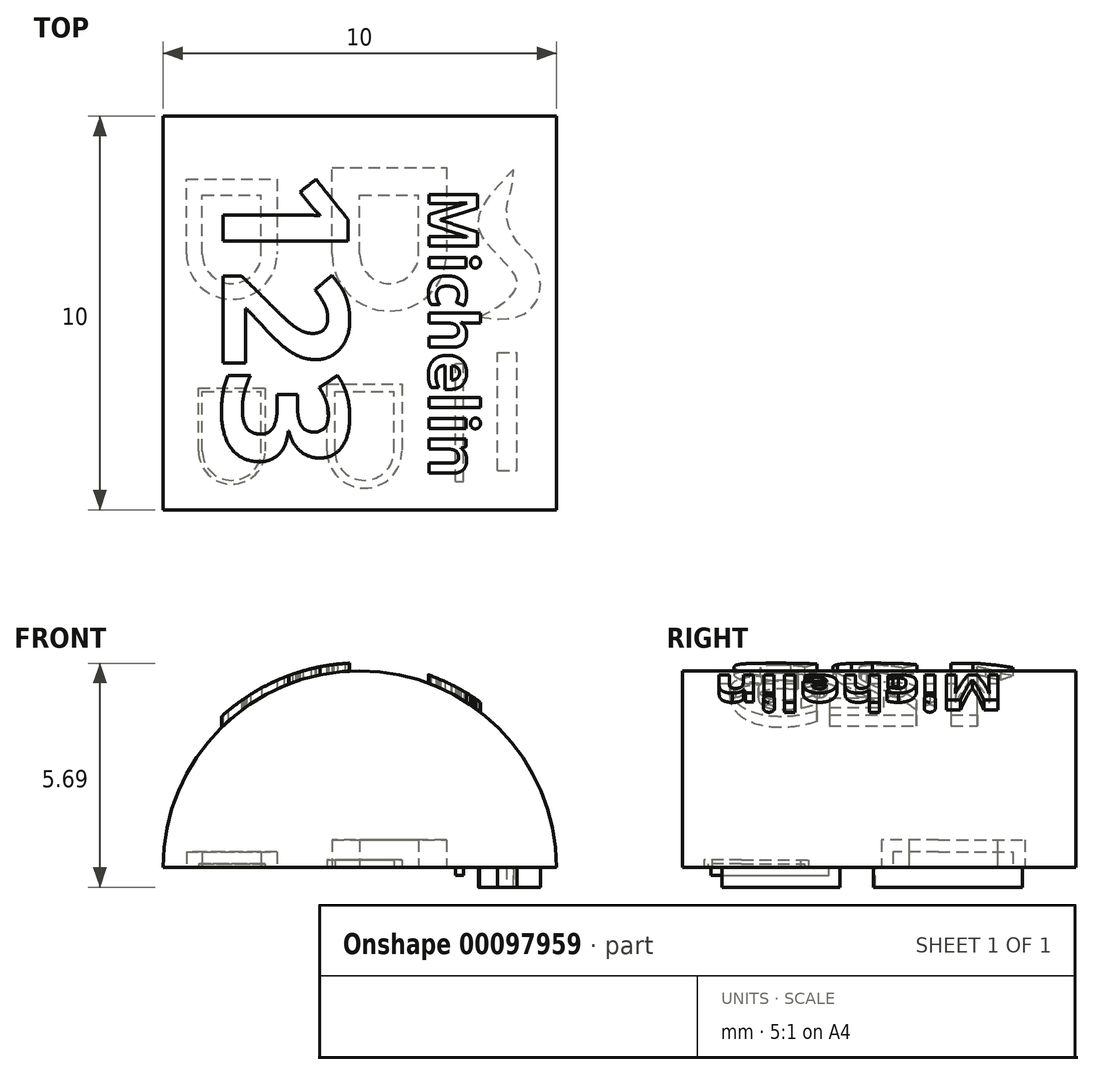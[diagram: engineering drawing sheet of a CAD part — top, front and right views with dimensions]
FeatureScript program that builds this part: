
annotation { "Feature Type Name" : "Feature", "Feature Type Description" : "" }
export const myFeature = defineFeature(function(context is Context, id is Id, definition is map)
    precondition{}
    {
        {
            var Q0;
            Q0=qCreatedBy(makeId("Front.planeOp"),FACE);
            var sketch = newSketch(context, id + "F0", { "sketchPlane" : qUnion([Q0])});
            skArc(sketch, "E0", {"start": v(-5, 0) * mm, "mid": v(0, 5) * mm, "end": v(5, 0) * mm});
            skLineSegment(sketch, "E1", {"start": v(-5, 0) * mm, "end": v(5, 0) * mm});
            skSolve(sketch);
        }
        {
            var Q0;
            Q0 = qSketchRegion(id + "F0", true);
            extrude(context, id + "F1", {"entities" : qUnion([Q0]), "depth" : 10 * mm});
        }
        {
            var Q0;
            Q0=makeQuery(id+"F1.opExtrude","CAP_FACE",FACE,{"disambiguationData":[OSD([sQuery(id+"F0.wireOp",EDGE,"E0"),sQuery(id+"F0.wireOp",EDGE,"E1")])],"isStart":false});
            var sketch = newSketch(context, id + "F2", { "sketchPlane" : qUnion([Q0])});
            skArc(sketch, "E2", {"start": v(-5.2, -0.07) * mm, "mid": v(-0.07, 5.2) * mm, "end": v(5.2, 0.07) * mm});
            skSolve(sketch);
        }
        {
            var Q0;
            Q0 = qSketchRegion(id + "F2", true);
            var Q1;
            Q1=sQuery(id+"F2.wireOp",EDGE,"E2");
            extrude(context, id + "F3", {"entities" : qUnion([Q0]), "bodyType" : ToolBodyType.SURFACE, "surfaceEntities" : qUnion([Q1]), "oppositeDirection" : true, "depth" : 10 * mm});
        }
        {
            var Q0;
            Q0=makeQuery(id+"F1.opExtrude","SWEPT_FACE",FACE,{"disambiguationData":[OSD([sQuery(id+"F0.wireOp",EDGE,"E1")])]});
            var sketch = newSketch(context, id + "F4", { "sketchPlane" : qUnion([Q0])});
            skLineSegment(sketch, "E3.top", {"start": v(-4, 7) * mm, "end": v(-2.5, 7) * mm});
            skLineSegment(sketch, "E3.left", {"start": v(-4, 8.5) * mm, "end": v(-4, 7) * mm});
            skLineSegment(sketch, "E4", {"start": v(-4.1, 8.5) * mm, "end": v(-4.1, 6.9) * mm});
            skLineSegment(sketch, "E5", {"start": v(-4.1, 6.9) * mm, "end": v(-2.4, 6.9) * mm});
            skLineSegment(sketch, "E6", {"start": v(-2.4, 6.9) * mm, "end": v(-2.4, 8.5) * mm});
            skLineSegment(sketch, "E7", {"start": v(-4.52, 8.5) * mm, "end": v(-2.4, 8.5) * mm, "construction": true});
            skLineSegment(sketch, "E8", {"start": v(-3.25, 8.9) * mm, "end": v(-3.25, 8.02) * mm, "construction": true});
            skArc(sketch, "E9", {"start": v(-4, 8.5) * mm, "mid": v(-3.25, 9.25) * mm, "end": v(-2.5, 8.5) * mm});
            skArc(sketch, "E10", {"start": v(-4.1, 8.5) * mm, "mid": v(-3.25, 9.35) * mm, "end": v(-2.4, 8.5) * mm});
            skLineSegment(sketch, "E11", {"start": v(-2.5, 8.5) * mm, "end": v(-2.5, 7) * mm});
            skSolve(sketch);
        }
        {
            var Q0;
            Q0=makeQuery(id+"F4.imprint","IMPRINT",FACE,{"disambiguationData":[TD([[makeQuery(id+"F4.imprint","IMPRINT",EDGE,{"derivedFrom":sQuery(id+"F4.wireOp",EDGE,"E3.top")}),-1.0]])]});
            extrude(context, id + "F5", {"entities" : qUnion([Q0]), "operationType" : NewBodyOperationType.REMOVE, "oppositeDirection" : true, "depth" : 0.1 * mm});
        }
        {
            var Q0;
            {var subQ0=sQuery(id+"F0.wireOp",EDGE,"E0");var subQ1=sQuery(id+"F0.wireOp",EDGE,"E1");Q0=makeQuery(id+"F5.boolean.opBoolean","SPLIT",FACE,{"disambiguationData":[TD([makeQuery(id+"F1.opExtrude","SWEPT_FACE",FACE,{"disambiguationData":[OSD([subQ0])]})])],"derivedFrom":makeQuery(id+"F1.opExtrude","SWEPT_FACE",FACE,{"disambiguationData":[OSD([subQ1])]})});}
            var sketch = newSketch(context, id + "F6", { "sketchPlane" : qUnion([Q0])});
            skLineSegment(sketch, "E12.top", {"start": v(-0.63, 7) * mm, "end": v(0.87, 7) * mm});
            skLineSegment(sketch, "E12.left", {"start": v(-0.63, 8.5) * mm, "end": v(-0.63, 7) * mm});
            skLineSegment(sketch, "E13", {"start": v(-0.83, 8.5) * mm, "end": v(-0.83, 6.8) * mm});
            skLineSegment(sketch, "E14", {"start": v(-0.83, 6.8) * mm, "end": v(1.07, 6.8) * mm});
            skLineSegment(sketch, "E15", {"start": v(1.07, 6.8) * mm, "end": v(1.07, 8.5) * mm});
            skLineSegment(sketch, "E16", {"start": v(-1.25, 8.5) * mm, "end": v(1.07, 8.5) * mm, "construction": true});
            skLineSegment(sketch, "E17", {"start": v(0.12, 8.8) * mm, "end": v(0.12, 7.92) * mm, "construction": true});
            skArc(sketch, "E18", {"start": v(-0.63, 8.5) * mm, "mid": v(0.12, 9.25) * mm, "end": v(0.87, 8.5) * mm});
            skArc(sketch, "E19", {"start": v(-0.83, 8.5) * mm, "mid": v(0.12, 9.45) * mm, "end": v(1.07, 8.5) * mm});
            skLineSegment(sketch, "E20", {"start": v(0.87, 8.5) * mm, "end": v(0.87, 7) * mm});
            skSolve(sketch);
        }
        {
            var Q0;
            Q0 = qSketchRegion(id + "F6", true);
            extrude(context, id + "F7", {"entities" : qUnion([Q0]), "operationType" : NewBodyOperationType.REMOVE, "oppositeDirection" : true, "depth" : 0.2 * mm});
        }
        {
            var Q0;
            {var subQ1=sQuery(id+"F0.wireOp",EDGE,"E0");var subQ2=makeQuery(id+"F1.opExtrude","SWEPT_FACE",FACE,{"disambiguationData":[OSD([subQ1])]});var subQ4=sQuery(id+"F0.wireOp",EDGE,"E1");Q0=makeQuery(id+"F7.boolean.opBoolean","SPLIT",FACE,{"disambiguationData":[TD([subQ2])],"derivedFrom":makeQuery(id+"F5.boolean.opBoolean","SPLIT",FACE,{"disambiguationData":[TD([subQ2])],"derivedFrom":makeQuery(id+"F1.opExtrude","SWEPT_FACE",FACE,{"disambiguationData":[OSD([subQ4])]})})});}
            var sketch = newSketch(context, id + "F8", { "sketchPlane" : qUnion([Q0])});
            skLineSegment(sketch, "E21.top", {"start": v(-4, 2) * mm, "end": v(-2.5, 2) * mm});
            skLineSegment(sketch, "E21.left", {"start": v(-4, 3.5) * mm, "end": v(-4, 2) * mm});
            skLineSegment(sketch, "E22", {"start": v(-4.4, 3.5) * mm, "end": v(-4.4, 1.6) * mm});
            skLineSegment(sketch, "E23", {"start": v(-4.4, 1.6) * mm, "end": v(-2.1, 1.6) * mm});
            skLineSegment(sketch, "E24", {"start": v(-2.1, 1.6) * mm, "end": v(-2.1, 3.5) * mm});
            skLineSegment(sketch, "E25", {"start": v(-3.84, 3.5) * mm, "end": v(-2.1, 3.5) * mm, "construction": true});
            skLineSegment(sketch, "E26", {"start": v(-3.25, 3.9) * mm, "end": v(-3.25, 3.02) * mm, "construction": true});
            skArc(sketch, "E27", {"start": v(-4, 3.5) * mm, "mid": v(-3.25, 4.25) * mm, "end": v(-2.5, 3.5) * mm});
            skArc(sketch, "E28", {"start": v(-4.4, 3.5) * mm, "mid": v(-3.25, 4.65) * mm, "end": v(-2.1, 3.5) * mm});
            skLineSegment(sketch, "E29", {"start": v(-2.5, 3.5) * mm, "end": v(-2.5, 2) * mm});
            skSolve(sketch);
        }
        {
            var Q0;
            Q0 = qSketchRegion(id + "F8", true);
            extrude(context, id + "F9", {"entities" : qUnion([Q0]), "operationType" : NewBodyOperationType.REMOVE, "oppositeDirection" : true, "depth" : 0.4 * mm});
        }
        {
            var Q0;
            {var subQ3=sQuery(id+"F0.wireOp",EDGE,"E0");var subQ4=makeQuery(id+"F1.opExtrude","SWEPT_FACE",FACE,{"disambiguationData":[OSD([subQ3])]});var subQ7=sQuery(id+"F0.wireOp",EDGE,"E1");Q0=makeQuery(id+"F9.boolean.opBoolean","SPLIT",FACE,{"disambiguationData":[TD([subQ4])],"derivedFrom":makeQuery(id+"F7.boolean.opBoolean","SPLIT",FACE,{"disambiguationData":[TD([subQ4])],"derivedFrom":makeQuery(id+"F5.boolean.opBoolean","SPLIT",FACE,{"disambiguationData":[TD([subQ4])],"derivedFrom":makeQuery(id+"F1.opExtrude","SWEPT_FACE",FACE,{"disambiguationData":[OSD([subQ7])]})})})});}
            var sketch = newSketch(context, id + "F10", { "sketchPlane" : qUnion([Q0])});
            skLineSegment(sketch, "E30.top", {"start": v(0, 2) * mm, "end": v(1.5, 2) * mm});
            skLineSegment(sketch, "E30.left", {"start": v(0, 3.5) * mm, "end": v(0, 2) * mm});
            skLineSegment(sketch, "E31", {"start": v(-0.7, 3.5) * mm, "end": v(-0.7, 1.3) * mm});
            skLineSegment(sketch, "E32", {"start": v(-0.7, 1.3) * mm, "end": v(2.2, 1.3) * mm});
            skLineSegment(sketch, "E33", {"start": v(2.2, 1.3) * mm, "end": v(2.2, 3.5) * mm});
            skLineSegment(sketch, "E34", {"start": v(-2.22, 3.5) * mm, "end": v(2.2, 3.5) * mm, "construction": true});
            skLineSegment(sketch, "E35", {"start": v(0.75, 3.9) * mm, "end": v(0.75, 3.02) * mm, "construction": true});
            skArc(sketch, "E36", {"start": v(0, 3.5) * mm, "mid": v(0.75, 4.25) * mm, "end": v(1.5, 3.5) * mm});
            skArc(sketch, "E37", {"start": v(-0.7, 3.5) * mm, "mid": v(0.75, 4.95) * mm, "end": v(2.2, 3.5) * mm});
            skLineSegment(sketch, "E38", {"start": v(1.5, 3.5) * mm, "end": v(1.5, 2) * mm});
            skSolve(sketch);
        }
        {
            var Q0;
            Q0 = qSketchRegion(id + "F10", true);
            extrude(context, id + "F11", {"entities" : qUnion([Q0]), "operationType" : NewBodyOperationType.REMOVE, "oppositeDirection" : true, "depth" : 0.7 * mm});
        }
        {
            var Q0;
            {var subQ4=sQuery(id+"F0.wireOp",EDGE,"E0");var subQ5=makeQuery(id+"F1.opExtrude","SWEPT_FACE",FACE,{"disambiguationData":[OSD([subQ4])]});var subQ8=sQuery(id+"F0.wireOp",EDGE,"E1");Q0=makeQuery(id+"F11.boolean.opBoolean","SPLIT",FACE,{"disambiguationData":[TD([subQ5])],"derivedFrom":makeQuery(id+"F9.boolean.opBoolean","SPLIT",FACE,{"disambiguationData":[TD([subQ5])],"derivedFrom":makeQuery(id+"F7.boolean.opBoolean","SPLIT",FACE,{"disambiguationData":[TD([subQ5])],"derivedFrom":makeQuery(id+"F5.boolean.opBoolean","SPLIT",FACE,{"disambiguationData":[TD([subQ5])],"derivedFrom":makeQuery(id+"F1.opExtrude","SWEPT_FACE",FACE,{"disambiguationData":[OSD([subQ8])]})})})})});}
            var sketch = newSketch(context, id + "F12", { "sketchPlane" : qUnion([Q0])});
            skLineSegment(sketch, "E39.bottom", {"start": v(2.44, 9.28) * mm, "end": v(2.64, 9.28) * mm});
            skLineSegment(sketch, "E39.top", {"start": v(2.44, 6.28) * mm, "end": v(2.64, 6.28) * mm});
            skLineSegment(sketch, "E39.left", {"start": v(2.44, 9.28) * mm, "end": v(2.44, 6.28) * mm});
            skLineSegment(sketch, "E39.right", {"start": v(2.64, 9.28) * mm, "end": v(2.64, 6.28) * mm});
            skSolve(sketch);
        }
        {
            var Q0;
            Q0=makeQuery(id+"F12.imprint","IMPRINT",FACE,{"disambiguationData":[TD([[makeQuery(id+"F12.imprint","IMPRINT",EDGE,{"derivedFrom":sQuery(id+"F12.wireOp",EDGE,"E39.bottom")}),-1.0]])]});
            extrude(context, id + "F13", {"entities" : qUnion([Q0]), "operationType" : NewBodyOperationType.ADD, "depth" : 0.2 * mm});
        }
        {
            var Q0;
            {var subQ4=sQuery(id+"F0.wireOp",EDGE,"E0");var subQ5=makeQuery(id+"F1.opExtrude","SWEPT_FACE",FACE,{"disambiguationData":[OSD([subQ4])]});var subQ8=sQuery(id+"F0.wireOp",EDGE,"E1");Q0=makeQuery(id+"F11.boolean.opBoolean","SPLIT",FACE,{"disambiguationData":[TD([subQ5])],"derivedFrom":makeQuery(id+"F9.boolean.opBoolean","SPLIT",FACE,{"disambiguationData":[TD([subQ5])],"derivedFrom":makeQuery(id+"F7.boolean.opBoolean","SPLIT",FACE,{"disambiguationData":[TD([subQ5])],"derivedFrom":makeQuery(id+"F5.boolean.opBoolean","SPLIT",FACE,{"disambiguationData":[TD([subQ5])],"derivedFrom":makeQuery(id+"F1.opExtrude","SWEPT_FACE",FACE,{"disambiguationData":[OSD([subQ8])]})})})})});}
            var sketch = newSketch(context, id + "F14", { "sketchPlane" : qUnion([Q0])});
            skLineSegment(sketch, "E40.bottom", {"start": v(3.5, 9) * mm, "end": v(4, 9) * mm});
            skLineSegment(sketch, "E40.top", {"start": v(3.5, 6) * mm, "end": v(4, 6) * mm});
            skLineSegment(sketch, "E40.left", {"start": v(3.5, 9) * mm, "end": v(3.5, 6) * mm});
            skLineSegment(sketch, "E40.right", {"start": v(4, 9) * mm, "end": v(4, 6) * mm});
            skSolve(sketch);
        }
        {
            var Q0;
            Q0 = qSketchRegion(id + "F14", true);
            extrude(context, id + "F15", {"entities" : qUnion([Q0]), "operationType" : NewBodyOperationType.ADD, "depth" : 0.5 * mm});
        }
        {
            var Q0;
            {var subQ4=sQuery(id+"F0.wireOp",EDGE,"E0");var subQ5=makeQuery(id+"F1.opExtrude","SWEPT_FACE",FACE,{"disambiguationData":[OSD([subQ4])]});var subQ8=sQuery(id+"F0.wireOp",EDGE,"E1");Q0=makeQuery(id+"F11.boolean.opBoolean","SPLIT",FACE,{"disambiguationData":[TD([subQ5])],"derivedFrom":makeQuery(id+"F9.boolean.opBoolean","SPLIT",FACE,{"disambiguationData":[TD([subQ5])],"derivedFrom":makeQuery(id+"F7.boolean.opBoolean","SPLIT",FACE,{"disambiguationData":[TD([subQ5])],"derivedFrom":makeQuery(id+"F5.boolean.opBoolean","SPLIT",FACE,{"disambiguationData":[TD([subQ5])],"derivedFrom":makeQuery(id+"F1.opExtrude","SWEPT_FACE",FACE,{"disambiguationData":[OSD([subQ8])]})})})})});}
            var sketch = newSketch(context, id + "F16", { "sketchPlane" : qUnion([Q0])});
            skFitSpline(sketch, "E41", {"points": [v(3.04, 5.1) * mm, v(4, 4.18) * mm, v(3.04, 2.9) * mm, v(3.9, 1.36) * mm], "startDerivative": vector(5.2, -2.73) * mm, "endDerivative": vector(4.38, -4.45) * mm});
            skFitSpline(sketch, "E42", {"points": [v(3.04, 5.1) * mm, v(3.98, 5.1) * mm, v(4.54, 4.6) * mm, v(4.46, 3.71) * mm, v(4.04, 3.24) * mm, v(3.73, 2.44) * mm, v(3.9, 1.36) * mm], "startDerivative": vector(5.56, 0.7) * mm, "endDerivative": vector(-0.3, -6.75) * mm});
            skSolve(sketch);
        }
        {
            var Q0;
            Q0 = qSketchRegion(id + "F16", true);
            extrude(context, id + "F17", {"entities" : qUnion([Q0]), "operationType" : NewBodyOperationType.ADD, "depth" : 0.5 * mm});
        }
        {
            var Q0;
            {var subQ4=sQuery(id+"F0.wireOp",EDGE,"E0");var subQ5=makeQuery(id+"F1.opExtrude","SWEPT_FACE",FACE,{"disambiguationData":[OSD([subQ4])]});var subQ8=sQuery(id+"F0.wireOp",EDGE,"E1");Q0=makeQuery(id+"F11.boolean.opBoolean","SPLIT",FACE,{"disambiguationData":[TD([subQ5])],"derivedFrom":makeQuery(id+"F9.boolean.opBoolean","SPLIT",FACE,{"disambiguationData":[TD([subQ5])],"derivedFrom":makeQuery(id+"F7.boolean.opBoolean","SPLIT",FACE,{"disambiguationData":[TD([subQ5])],"derivedFrom":makeQuery(id+"F5.boolean.opBoolean","SPLIT",FACE,{"disambiguationData":[TD([subQ5])],"derivedFrom":makeQuery(id+"F1.opExtrude","SWEPT_FACE",FACE,{"disambiguationData":[OSD([subQ8])]})})})})});}
            var Q1;
            Q1 = qBodyType(qCreatedBy(id + "F9Fqc22qCZveZrP_2" ,EDGE), BodyType.WIRE);
            cPlane(context, id + "F18", {"entities" : qUnion([Q0, Q1]), "cplaneType" : CPlaneType.OFFSET, "offset" : 8 * mm, "oppositeDirection" : true, "width" : 150 * mm, "height" : 150 * mm});
        }
        {
            var Q0;
            {var subQ0=sQuery(id+"F0.wireOp",EDGE,"E1");var subQ1=sQuery(id+"F0.wireOp",EDGE,"E0");Q0=makeQuery(id+"F1.opExtrude","SWEPT_EDGE",EDGE,{"disambiguationData":[OSD([subQ1,subQ0]),TDD([makeQuery(id+"F0.imprint","INTERSECT",VERTEX,{"disambiguationData":[OD(0.0)],"derivedFrom":[subQ1,subQ0]})])]});}
            cPlane(context, id + "F19", {"entities" : qUnion([Q0]), "cplaneType" : CPlaneType.LINE_ANGLE, "offset" : 25 * mm, "angle" : 0 * degree, "width" : 150 * mm, "height" : 150 * mm});
        }
        {
            var Q0;
            Q0=qCreatedBy(id+"F19.planeOp",FACE);
            var sketch = newSketch(context, id + "F20", { "sketchPlane" : qUnion([Q0])});
            skText(sketch, "E43", { "text": "Michelin", "fontName": "OpenSans-Bold.ttf"});
            skText(sketch, "E44", { "text": "123", "fontName": "OpenSans-Bold.ttf"});
            const initialGuessF20  = {"E43": [0.00176, -0.00183, 0, -1, 0.00124], "E44": [-0.00347, -0.00134, 0, -1, 0.0032]};
            skSetInitialGuess(sketch, initialGuessF20);
            skSolve(sketch);
        }
        {
            var Q0;
            Q0 = qSketchRegion(id + "F20", true);
            var Q1;
            Q1=makeQuery(id+"F3.opExtrude","SWEPT_FACE",FACE,{"disambiguationData":[OSD([sQuery(id+"F2.wireOp",EDGE,"E2")])]});
            var Q2;
            Q2=makeQuery(id+"F1.opExtrude","SWEPT_FACE",FACE,{"disambiguationData":[OSD([sQuery(id+"F0.wireOp",EDGE,"E0")])]});
            extrude(context, id + "F21", {"entities" : qUnion([Q0]), "operationType" : NewBodyOperationType.ADD, "endBound" : BoundingType.UP_TO_SURFACE, "endBoundEntityFace" : qUnion([Q1]), "depth" : 25 * mm, "hasSecondDirection" : true, "secondDirectionBound" : SecondDirectionBoundingType.UP_TO_SURFACE, "secondDirectionOppositeDirection" : false, "secondDirectionBoundEntityFace" : qUnion([Q2]), "secondDirectionDepth" : 25 * mm});
        }
    });
